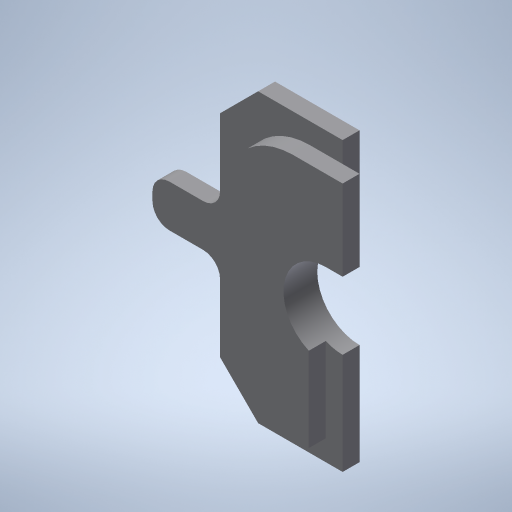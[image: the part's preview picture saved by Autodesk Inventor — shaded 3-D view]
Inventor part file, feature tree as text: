
AUTODESK INVENTOR PART (.ipt)
format: ipt  version: 2023.3 (Build 273359000, 359)  size: 315,904 bytes
history: native  units: mm
features: sketch x5, extrude x4, hole x1, fillet x1, thicken_offset x1, projected_geometry x1
ambient origin geometry x8: Origin, YZ Plane, XZ Plane, XY Plane, X Axis, Y Axis, Z Axis, Center Point
bodies: Solid1 (feature_tree)
feature tree (13):
  extrude  "Extrusion1"  Depth=34.0mm
  hole  "Hole1"  [1 undecoded]
  extrude  "Extrusion2"  Depth=4.5mm
  extrude  "Extrusion3"  Depth=4.5mm
  extrude  "Extrusion4"  Depth=2.0mm
  fillet  "Fillet1"  Radius=2.0mm
  thicken_offset  "Thicken1"
  sketch  "Sketch1"  dims[d0=29.0mm d1=34.0mm]
  sketch  "Sketch2"  dims[d2=4.5mm d3=4.5mm]
  sketch  "Sketch3"  dims[d4=4.5mm d5=4.5mm]
  sketch  "Sketch4"  dims[d6=4.5mm d7=4.5mm]
  sketch  "Sketch5"  dims[d8=4.5mm d9=4.5mm d10=2.0mm d11=0.0mm d12=10.0mm d13=6.0mm d14=4.0mm d15=2.0mm d16=90.0deg d17=1.0mm d18=0.0mm d19=29.7mm d20=24.7mm d21=8.5mm d22=2.0mm d23=0.0mm d24=0.0mm d25=0.0mm d26=2.0mm d27=0.0mm d28=2.0mm d29=0.0mm d30=2.0mm d31=2.0mm d32=8.0mm d33=5.0mm d34=2.0mm d35=0.3mm d36=0.3mm]
  projected_geometry  "Projected Loop1"
note: 1 required parameter value undecoded (feature->parameter linkage not recoverable at this tier; creation-order binding heuristic only, values carry confidence <= 0.55)
